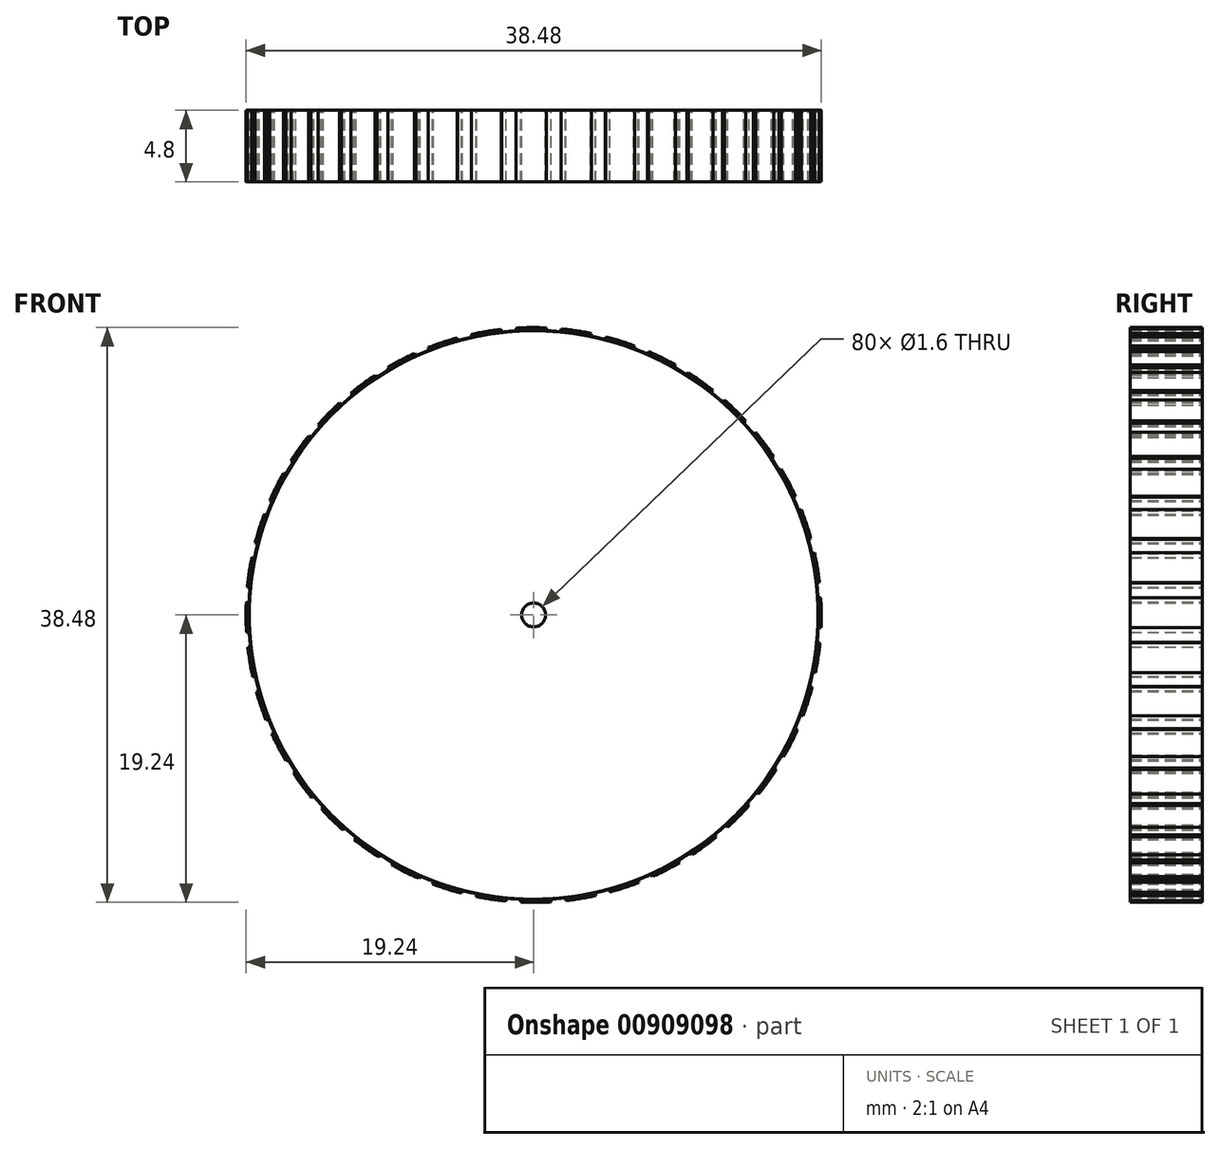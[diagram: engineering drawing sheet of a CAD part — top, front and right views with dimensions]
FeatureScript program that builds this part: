
annotation { "Feature Type Name" : "Feature", "Feature Type Description" : "" }
export const myFeature = defineFeature(function(context is Context, id is Id, definition is map)
    precondition{}
    {
        {
            var Q0;
            Q0=qCreatedBy(makeId("Front.planeOp"),FACE);
            var sketch = newSketch(context, id + "F0", { "sketchPlane" : qUnion([Q0])});
            skCircle(sketch, "E0", {"center": v(0, 0) * mm, "radius": 19.05 * mm});
            skCircle(sketch, "E1", {"center": v(0, 0) * mm, "radius": 19.24 * mm});
            skLineSegment(sketch, "E2", {"start": v(-12.98, 14.2) * mm, "end": v(-12.86, 14.06) * mm});
            skCircle(sketch, "E3", {"center": v(0, 0) * mm, "radius": 0.8 * mm});
            skLineSegment(sketch, "E4", {"start": v(-11.44, 15.47) * mm, "end": v(-11.33, 15.32) * mm});
            skLineSegment(sketch, "E5.1.0", {"start": v(-15.65, 11.2) * mm, "end": v(-15.5, 11.08) * mm});
            skLineSegment(sketch, "E5.1.1", {"start": v(-14.4, 12.75) * mm, "end": v(-14.26, 12.63) * mm});
            skLineSegment(sketch, "E5.2.0", {"start": v(-17.64, 7.7) * mm, "end": v(-17.46, 7.61) * mm});
            skLineSegment(sketch, "E5.2.1", {"start": v(-16.74, 9.48) * mm, "end": v(-16.58, 9.39) * mm});
            skLineSegment(sketch, "E5.3.0", {"start": v(-18.85, 3.86) * mm, "end": v(-18.66, 3.82) * mm});
            skLineSegment(sketch, "E5.3.1", {"start": v(-18.35, 5.8) * mm, "end": v(-18.17, 5.73) * mm});
            skLineSegment(sketch, "E5.4.0", {"start": v(-19.24, -0.15) * mm, "end": v(-19.05, -0.15) * mm});
            skLineSegment(sketch, "E5.4.1", {"start": v(-19.15, 1.85) * mm, "end": v(-18.96, 1.83) * mm});
            skLineSegment(sketch, "E5.5.0", {"start": v(-18.79, -4.14) * mm, "end": v(-18.6, -4.1) * mm});
            skLineSegment(sketch, "E5.5.1", {"start": v(-19.12, -2.17) * mm, "end": v(-18.93, -2.15) * mm});
            skLineSegment(sketch, "E5.6.0", {"start": v(-17.52, -7.96) * mm, "end": v(-17.34, -7.88) * mm});
            skLineSegment(sketch, "E5.6.1", {"start": v(-18.25, -6.1) * mm, "end": v(-18.07, -6.04) * mm});
            skLineSegment(sketch, "E5.7.0", {"start": v(-15.48, -11.43) * mm, "end": v(-15.33, -11.32) * mm});
            skLineSegment(sketch, "E5.7.1", {"start": v(-16.58, -9.76) * mm, "end": v(-16.42, -9.66) * mm});
            skLineSegment(sketch, "E5.8.0", {"start": v(-12.76, -14.4) * mm, "end": v(-12.64, -14.25) * mm});
            skLineSegment(sketch, "E5.8.1", {"start": v(-14.2, -13) * mm, "end": v(-14.05, -12.87) * mm});
            skLineSegment(sketch, "E5.9.0", {"start": v(-9.5, -16.74) * mm, "end": v(-9.4, -16.57) * mm});
            skLineSegment(sketch, "E5.9.1", {"start": v(-11.18, -15.66) * mm, "end": v(-11.07, -15.5) * mm});
            skLineSegment(sketch, "E5.10.0", {"start": v(-5.8, -18.34) * mm, "end": v(-5.75, -18.16) * mm});
            skLineSegment(sketch, "E5.10.1", {"start": v(-7.68, -17.64) * mm, "end": v(-7.6, -17.47) * mm});
            skLineSegment(sketch, "E5.11.0", {"start": v(-1.86, -19.15) * mm, "end": v(-1.85, -18.96) * mm});
            skLineSegment(sketch, "E5.11.1", {"start": v(-3.84, -18.85) * mm, "end": v(-3.8, -18.67) * mm});
            skLineSegment(sketch, "E5.12.0", {"start": v(2.16, -19.12) * mm, "end": v(2.14, -18.93) * mm});
            skLineSegment(sketch, "E5.12.1", {"start": v(0.16, -19.24) * mm, "end": v(0.16, -19.05) * mm});
            skLineSegment(sketch, "E5.13.0", {"start": v(6.09, -18.25) * mm, "end": v(6.03, -18.07) * mm});
            skLineSegment(sketch, "E5.13.1", {"start": v(4.16, -18.79) * mm, "end": v(4.12, -18.6) * mm});
            skLineSegment(sketch, "E5.14.0", {"start": v(9.75, -16.59) * mm, "end": v(9.65, -16.42) * mm});
            skLineSegment(sketch, "E5.14.1", {"start": v(7.97, -17.51) * mm, "end": v(7.9, -17.34) * mm});
            skLineSegment(sketch, "E5.15.0", {"start": v(12.98, -14.2) * mm, "end": v(12.86, -14.06) * mm});
            skLineSegment(sketch, "E5.15.1", {"start": v(11.44, -15.47) * mm, "end": v(11.33, -15.32) * mm});
            skLineSegment(sketch, "E5.16.0", {"start": v(15.65, -11.2) * mm, "end": v(15.5, -11.08) * mm});
            skLineSegment(sketch, "E5.16.1", {"start": v(14.4, -12.75) * mm, "end": v(14.26, -12.63) * mm});
            skLineSegment(sketch, "E5.17.0", {"start": v(17.64, -7.7) * mm, "end": v(17.46, -7.61) * mm});
            skLineSegment(sketch, "E5.17.1", {"start": v(16.74, -9.48) * mm, "end": v(16.58, -9.39) * mm});
            skLineSegment(sketch, "E5.18.0", {"start": v(18.85, -3.86) * mm, "end": v(18.66, -3.82) * mm});
            skLineSegment(sketch, "E5.18.1", {"start": v(18.35, -5.8) * mm, "end": v(18.17, -5.73) * mm});
            skLineSegment(sketch, "E5.19.0", {"start": v(19.24, 0.15) * mm, "end": v(19.05, 0.15) * mm});
            skLineSegment(sketch, "E5.19.1", {"start": v(19.15, -1.85) * mm, "end": v(18.96, -1.83) * mm});
            skLineSegment(sketch, "E5.20.0", {"start": v(18.79, 4.14) * mm, "end": v(18.6, 4.1) * mm});
            skLineSegment(sketch, "E5.20.1", {"start": v(19.12, 2.17) * mm, "end": v(18.93, 2.15) * mm});
            skLineSegment(sketch, "E5.21.0", {"start": v(17.52, 7.96) * mm, "end": v(17.34, 7.88) * mm});
            skLineSegment(sketch, "E5.21.1", {"start": v(18.25, 6.1) * mm, "end": v(18.07, 6.04) * mm});
            skLineSegment(sketch, "E5.22.0", {"start": v(15.48, 11.43) * mm, "end": v(15.33, 11.32) * mm});
            skLineSegment(sketch, "E5.22.1", {"start": v(16.58, 9.76) * mm, "end": v(16.42, 9.66) * mm});
            skLineSegment(sketch, "E5.23.0", {"start": v(12.76, 14.4) * mm, "end": v(12.64, 14.25) * mm});
            skLineSegment(sketch, "E5.23.1", {"start": v(14.2, 13) * mm, "end": v(14.05, 12.87) * mm});
            skLineSegment(sketch, "E5.24.0", {"start": v(9.5, 16.74) * mm, "end": v(9.4, 16.57) * mm});
            skLineSegment(sketch, "E5.24.1", {"start": v(11.18, 15.66) * mm, "end": v(11.07, 15.5) * mm});
            skLineSegment(sketch, "E5.25.0", {"start": v(5.8, 18.34) * mm, "end": v(5.75, 18.16) * mm});
            skLineSegment(sketch, "E5.25.1", {"start": v(7.68, 17.64) * mm, "end": v(7.6, 17.47) * mm});
            skLineSegment(sketch, "E5.26.0", {"start": v(1.86, 19.15) * mm, "end": v(1.85, 18.96) * mm});
            skLineSegment(sketch, "E5.26.1", {"start": v(3.84, 18.85) * mm, "end": v(3.8, 18.67) * mm});
            skLineSegment(sketch, "E5.27.0", {"start": v(-2.16, 19.12) * mm, "end": v(-2.14, 18.93) * mm});
            skLineSegment(sketch, "E5.27.1", {"start": v(-0.16, 19.24) * mm, "end": v(-0.16, 19.05) * mm});
            skLineSegment(sketch, "E5.28.0", {"start": v(-6.09, 18.25) * mm, "end": v(-6.03, 18.07) * mm});
            skLineSegment(sketch, "E5.28.1", {"start": v(-4.16, 18.79) * mm, "end": v(-4.12, 18.6) * mm});
            skLineSegment(sketch, "E5.29.0", {"start": v(-9.75, 16.59) * mm, "end": v(-9.65, 16.42) * mm});
            skLineSegment(sketch, "E5.29.1", {"start": v(-7.97, 17.51) * mm, "end": v(-7.9, 17.34) * mm});
            skSolve(sketch);
        }
        {
            var Q0;
            {var subQ0=sQuery(id+"F0.wireOp",EDGE,"E0");var subQ1=makeQuery(id+"F0.imprint","INTERSECT",VERTEX,{"derivedFrom":[subQ0,sQuery(id+"F0.wireOp",EDGE,"E2")]});Q0=makeQuery(id+"F0.imprint","IMPRINT",FACE,{"disambiguationData":[TD([[makeQuery(id+"F0.imprint","IMPRINT",EDGE,{"disambiguationData":[TD([[subQ1,-1.0]])],"derivedFrom":subQ0}),1.0]])]});}
            var Q1;
            {var subQ0=sQuery(id+"F0.wireOp",EDGE,"E2");Q1=makeQuery(id+"F0.imprint","IMPRINT",FACE,{"disambiguationData":[TD([[makeQuery(id+"F0.imprint","IMPRINT",EDGE,{"derivedFrom":subQ0}),-1.0]])]});}
            extrude(context, id + "F1", {"entities" : qUnion([Q0, Q1]), "depth" : 4.8 * mm, "offsetDistance" : 25.4 * mm});
        }
        {
            var Q0;
            Q0=qCreatedBy(makeId("Right.planeOp"),FACE);
            var sketch = newSketch(context, id + "F2", { "sketchPlane" : qUnion([Q0])});
            skLineSegment(sketch, "E6", {"start": v(0, 0) * mm, "end": v(-6, 0) * mm});
            skSolve(sketch);
        }
        {
            var Q0;
            Q0=makeQuery(id+"F1.opExtrude","SWEPT_BODY",BODY,{"disambiguationData":[OSD([sQuery(id+"F0.wireOp",EDGE,"E0"),sQuery(id+"F0.wireOp",EDGE,"E1"),sQuery(id+"F0.wireOp",EDGE,"E2"),sQuery(id+"F0.wireOp",EDGE,"gi7JvM5U-I49X-A4oP-xxIr-ycPihc2GaP59")])]});
            var Q1;
            Q1=sQuery(id+"F2.wireOp",EDGE,"E6");
            circularPattern(context, id + "F3", {"entities" : qUnion([Q0]), "axis" : qUnion([Q1]), "angle" : 360 * degree, "instanceCount" : 40, "equalSpace" : true});
        }
    });
